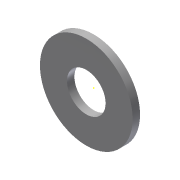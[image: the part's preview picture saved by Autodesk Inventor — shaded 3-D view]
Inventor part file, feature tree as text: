
AUTODESK INVENTOR PART (.ipt)
format: ipt  version: 2013 (Build 170138000, 138)  size: 90,112 bytes
history: native  units: in
note: dims shown in document units (in); Inventor stores cm internally (conversion verified against a paired STEP export)
features: sketch x2, extrude x1
ambient origin geometry x8: Origin, YZ Plane, XZ Plane, XY Plane, X Axis, Y Axis, Z Axis, Center Point
bodies: Solid1 (feature_tree)
feature tree (3):
  sketch  "Sketch1"  dims[d0=0.3125in d1=0.75in]
  extrude  "Extrusion1"  Depth=0.75in
  sketch  "Sketch2"  dims[d2=0.06in d3=0.0in]
